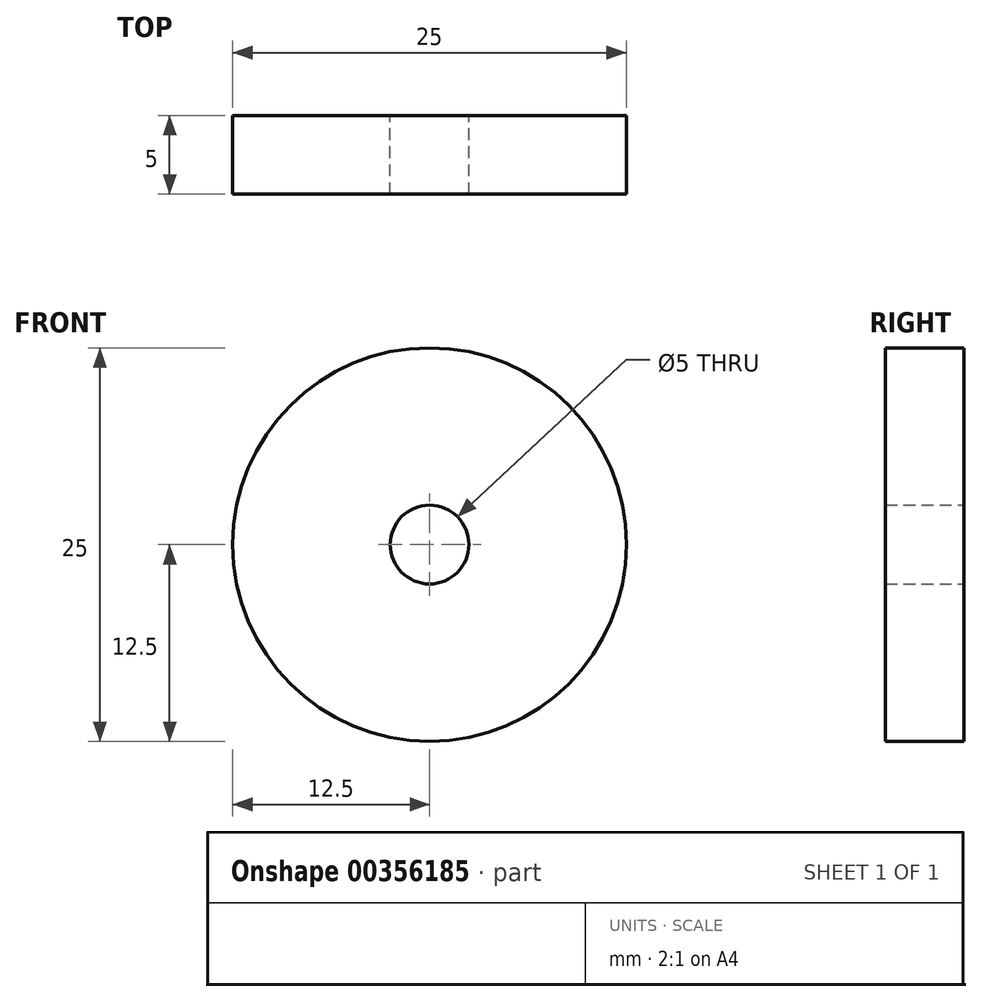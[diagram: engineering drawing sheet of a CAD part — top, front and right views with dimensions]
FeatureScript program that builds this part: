
annotation { "Feature Type Name" : "Feature", "Feature Type Description" : "" }
export const myFeature = defineFeature(function(context is Context, id is Id, definition is map)
    precondition{}
    {
        {
            var Q0;
            Q0=qCreatedBy(makeId("Front.planeOp"),FACE);
            var sketch = newSketch(context, id + "F0", { "sketchPlane" : qUnion([Q0])});
            skCircle(sketch, "E0", {"center": v(0, 0) * mm, "radius": 2.5 * mm});
            skCircle(sketch, "E1", {"center": v(0, 0) * mm, "radius": 12.5 * mm});
            skSolve(sketch);
        }
        {
            var Q0;
            Q0=makeQuery(id+"F0.imprint","IMPRINT",FACE,{"disambiguationData":[TD([[makeQuery(id+"F0.imprint","IMPRINT",EDGE,{"derivedFrom":sQuery(id+"F0.wireOp",EDGE,"E0")}),-1.0]])]});
            extrude(context, id + "F1", {"entities" : qUnion([Q0]), "depth" : 5 * mm});
        }
    });
